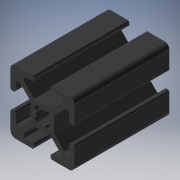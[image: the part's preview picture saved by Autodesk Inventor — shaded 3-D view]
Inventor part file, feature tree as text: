
AUTODESK INVENTOR PART (.ipt)
format: ipt  version: 2019 (Build 230136000, 136)  size: 236,032 bytes
history: native  units: mm
features: extrude x1, sketch x1
ambient origin geometry x8: Origin, YZ Plane, XZ Plane, XY Plane, X Axis, Y Axis, Z Axis, Center Point
bodies: Solid1 (feature_tree)
feature tree (2):
  extrude  "Extrusion1"  [1 undecoded]
  sketch  "Sketch_1"  dims[d0=30.0mm d1=0.0mm]
note: 1 required parameter value undecoded (feature->parameter linkage not recoverable at this tier; creation-order binding heuristic only, values carry confidence <= 0.55)
